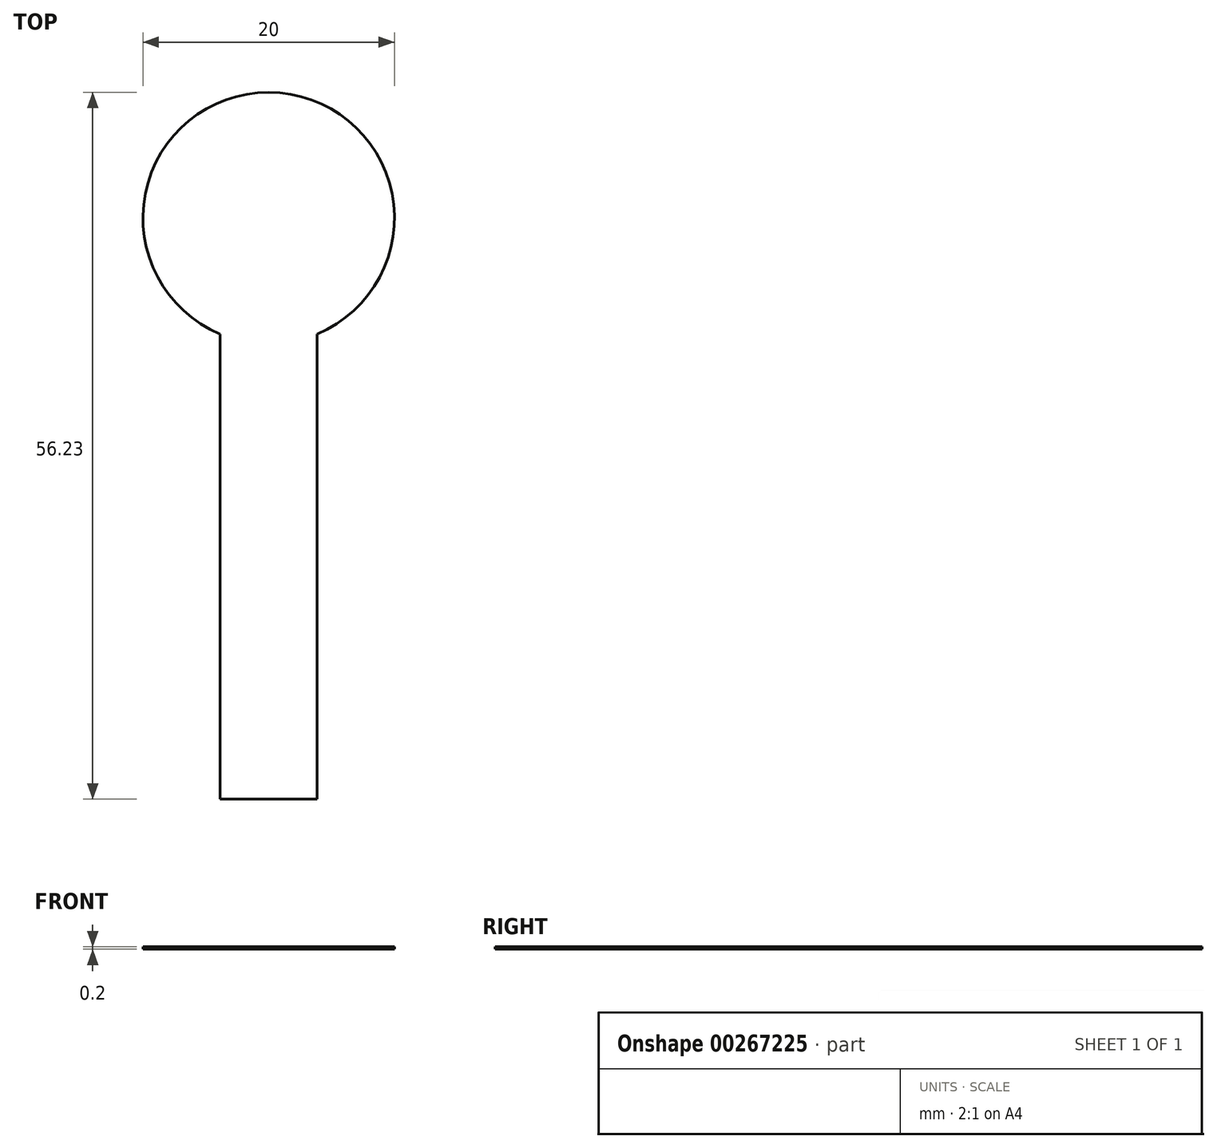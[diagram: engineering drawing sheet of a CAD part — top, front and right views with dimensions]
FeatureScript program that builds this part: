
annotation { "Feature Type Name" : "Feature", "Feature Type Description" : "" }
export const myFeature = defineFeature(function(context is Context, id is Id, definition is map)
    precondition{}
    {
        {
            var Q0;
            Q0=qCreatedBy(makeId("Top.planeOp"),FACE);
            var sketch = newSketch(context, id + "F0", { "sketchPlane" : qUnion([Q0])});
            skCircle(sketch, "E0", {"center": v(0, 0) * mm, "radius": 10 * mm});
            skLineSegment(sketch, "E1.bottom", {"start": v(3.85, -9.23) * mm, "end": v(-3.85, -9.23) * mm});
            skLineSegment(sketch, "E1.top", {"start": v(3.85, -46.23) * mm, "end": v(-3.85, -46.23) * mm});
            skLineSegment(sketch, "E1.left", {"start": v(3.85, -9.23) * mm, "end": v(3.85, -46.23) * mm});
            skLineSegment(sketch, "E1.right", {"start": v(-3.85, -9.23) * mm, "end": v(-3.85, -46.23) * mm});
            skPoint(sketch, "E1.middle", {"position": v(0, -27.73) * mm});
            skSolve(sketch);
        }
        {
            var Q0;
            {var subQ0=sQuery(id+"F0.wireOp",EDGE,"E1.bottom");Q0=makeQuery(id+"F0.imprint","IMPRINT",FACE,{"disambiguationData":[TD([[makeQuery(id+"F0.imprint","IMPRINT",EDGE,{"derivedFrom":subQ0}),-1.0]])]});}
            var Q1;
            Q1=makeQuery(id+"F0.imprint","IMPRINT",FACE,{"disambiguationData":[TD([[makeQuery(id+"F0.imprint","IMPRINT",EDGE,{"derivedFrom":sQuery(id+"F0.wireOp",EDGE,"E1.top")}),-1.0]])]});
            var Q2;
            {var subQ0=sQuery(id+"F0.wireOp",EDGE,"E1.bottom");Q2=makeQuery(id+"F0.imprint","IMPRINT",FACE,{"disambiguationData":[TD([[makeQuery(id+"F0.imprint","IMPRINT",EDGE,{"derivedFrom":subQ0}),1.0]])]});}
            extrude(context, id + "F1", {"entities" : qUnion([Q0, Q1, Q2]), "depth" : 0.2 * mm});
        }
    });
